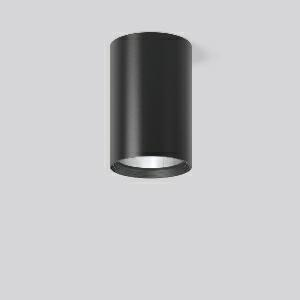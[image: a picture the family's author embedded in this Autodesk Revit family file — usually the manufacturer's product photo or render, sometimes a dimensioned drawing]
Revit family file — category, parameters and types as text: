
# Revit family: heledon_maxi_a_931224_003_e412
name_source: partatom
category: Lighting Fixtures
units: mm (PartAtom-declared; Revit-internal decimal feet)

## family parameters
Cut with Voids When Loaded = No
Host = Face
Light Source = No
Part Type = Normal
Room Calculation Point = No
Round Connector Dimension = Use Diameter
Shared = No

## types (1)
- HELEDON maxi A (1 x LED Modul 930, 4300 lm, 3000)
    Apparent Load = 35 VA
    Approval mark = CE
    CIE Flux Codes = 100 100 100 100 100
    Color Rendering = 90
    Color Temperature = 3000
    Default Elevation = 1800 mm
    Description = Series: HELEDON maxi
Cylindrical surface-mounted downlight. Housing: die-cast aluminium, powder-coated. Internal ceiling frame polycarbonate with bayonet mounting. Black plastic ring and recessed LED to prevent glare from the side. Optical assembly with reflector made of MIRO-Silver with 98% total light reflection for outstanding efficiency - can be changed without tools. Best colour rendering index Ra>90. Suitable for Ceiling mounting. Easy installation with a separate ceiling frame with bayonet mounting and plug connection. Driver integrated. Connected via plug-in connector. High quality converter without flickering and stroboscopic effect. The following accessories can be mounted without use of tools: interchangeable lenses, decorative glasses, honeycomb louvre, clear and frosted diffusers, white interchangeable plastic ring. 
Colour: deep black, matt (RAL 9005)
Diameter: 123 mm
Height: 183 mm
Lamp: LED
Socket: without socket
Colour temperature: 3000K
Colour rendering index (CRI): 92
System power: 35 W
Rated luminous flux: 4300 lm
Luminous efficiency: 123 lm/W
Control gear: Regulated power supply
Protection class: I
Type of protection: IP 20
    Height = 183 mm
    Lamp = 1 x LED Modul 930
    Lamp Light Flux = 4300 lm
    Lamp count = 1
    Length = 123 mm
    Lifetime = 50000 h
    Luminous efficacy = 123 lm/W
    Manufacturer = RZB
    ModVariant = No
    Model = 931224.003
    Mounting Place = Ceiling
    Mounting Type = Surface mounted
    Number of Poles = 1
    OnlyDefault = Yes
    Power Factor = 1
    Product Name = HELEDON maxi A
    Product group = Surface mounted downlights
    ProductGroupID = 302
    Protection Class = Protection class I
    Protection Degree = IP 20
    RLX_Detail_Level = 1
    RLX_Emergency_Light_Flux = 0 lm
    RLX_Emergency_Type = 0
    RLX_Emergency_Type_DB = No
    RlxData = <blob elided: 96277 chars, md5=75aca83d>
    Socket = socket
    Standby Power = 0 W
    System Light Flux = 4300 lm
    System Power = 35 W
    Type Comments = Product without accessories
    Type Image = 931192.003.jpg
    URL = http://relux.com
    VarID = ---
    Voltage = 230 V
    Voltage Range = 220-240 V
    Weight = 0.00 kg
    Width = 0 mm  [stored 0 ft]

note: [stored X ft] marks values corroborated as IEEE doubles in the binary element streams (Revit-internal decimal feet)

## geometry (parser evidence)
native form markers: Blend x4, Sweep x13
no freeform markers — native parametric forms only
